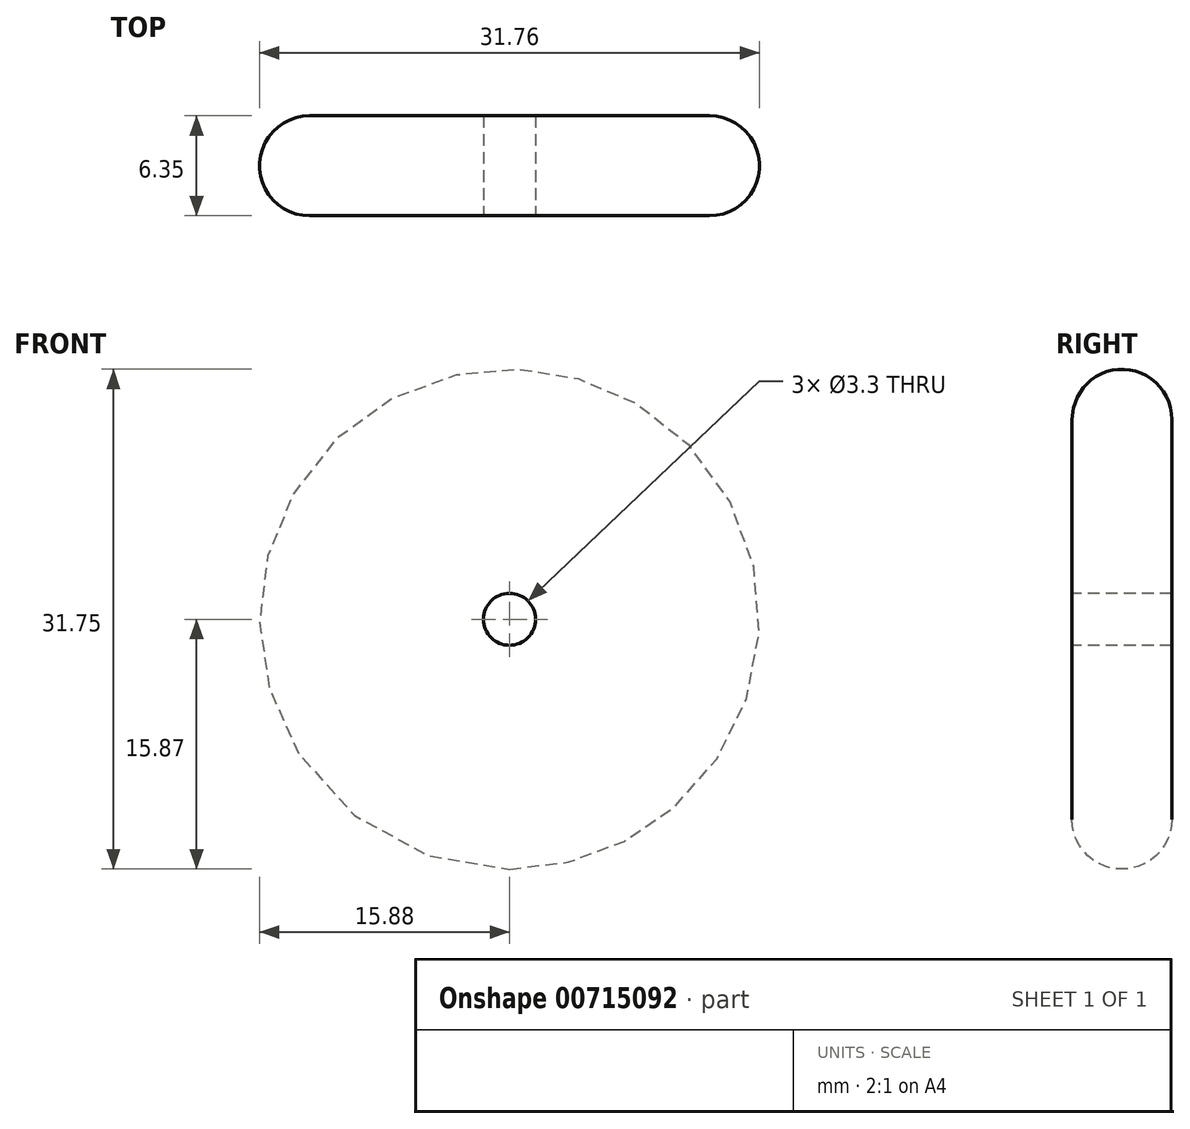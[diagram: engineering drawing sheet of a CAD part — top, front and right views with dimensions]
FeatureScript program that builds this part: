
annotation { "Feature Type Name" : "Feature", "Feature Type Description" : "" }
export const myFeature = defineFeature(function(context is Context, id is Id, definition is map)
    precondition{}
    {
        {
            var Q0;
            Q0=qCreatedBy(makeId("Front.planeOp"),FACE);
            var sketch = newSketch(context, id + "F0", { "sketchPlane" : qUnion([Q0])});
            skCircle(sketch, "E0", {"center": v(0, 0) * mm, "radius": 15.88 * mm});
            skSolve(sketch);
        }
        {
            var Q0;
            Q0=makeQuery(id+"F0.imprint","IMPRINT",FACE,{"disambiguationData":[TD([[makeQuery(id+"F0.imprint","IMPRINT",EDGE,{"derivedFrom":sQuery(id+"F0.wireOp",EDGE,"E0")}),1.0]])]});
            extrude(context, id + "F1", {"entities" : qUnion([Q0]), "depth" : 6.35 * mm, "offsetDistance" : 25.4 * mm});
        }
        {
            var Q0;
            Q0=makeQuery(id+"F1.opExtrude","CAP_FACE",FACE,{"disambiguationData":[OSD([sQuery(id+"F0.wireOp",EDGE,"E0")])],"isStart":false});
            var sketch = newSketch(context, id + "F2", { "sketchPlane" : qUnion([Q0])});
            skCircle(sketch, "E1", {"center": v(0, 0) * mm, "radius": 1.65 * mm});
            skSolve(sketch);
        }
        {
            var Q0;
            Q0=sQuery(id+"F2.wireOp",VERTEX,"E1.center");
            var Q1;
            Q1=makeQuery(id+"F1.opExtrude","SWEPT_BODY",BODY,{"disambiguationData":[OSD([sQuery(id+"F0.wireOp",EDGE,"E0")])]});
            hole(context, id + "F3", {"style" : HoleStyle.SIMPLE, "endStyle" : HoleEndStyle.THROUGH, "holeDiameter" : 3.3 * mm, "majorDiameter" : 6.35 * mm, "isTappedThrough" : true, "tappedDepth" : 12.7 * mm, "tapClearance" : 3, "locations" : qUnion([Q0]), "scope" : qUnion([Q1])});
        }
        {
            var Q0;
            Q0=makeQuery(id+"F1.opExtrude","CAP_EDGE",EDGE,{"disambiguationData":[OSD([sQuery(id+"F0.wireOp",EDGE,"E0")])],"isStart":false});
            var Q1;
            Q1=makeQuery(id+"F1.opExtrude","CAP_EDGE",EDGE,{"disambiguationData":[OSD([sQuery(id+"F0.wireOp",EDGE,"E0")])],"isStart":true});
            fillet(context, id + "F4", {"entities" : qUnion([Q0, Q1]), "radius" : 3.17 * mm, "tangentPropagation" : true, "allowEdgeOverflow" : false});
        }
    });
